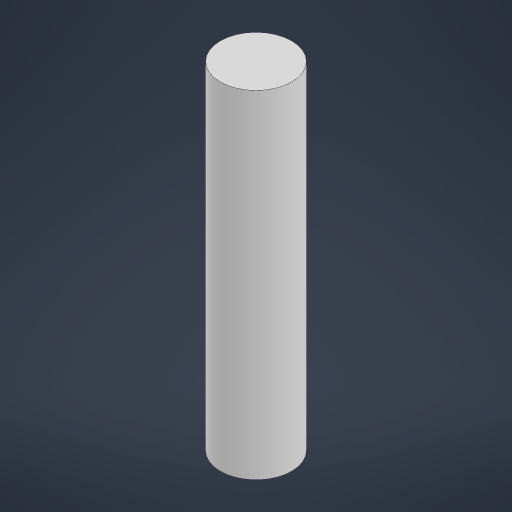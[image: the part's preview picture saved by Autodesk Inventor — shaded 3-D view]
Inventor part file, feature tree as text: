
AUTODESK INVENTOR PART (.ipt)
format: ipt  version: 2023 (Build 270158030, 158C)  size: 155,648 bytes
history: native  units: in
note: dims shown in document units (in); Inventor stores cm internally (conversion verified against a paired STEP export)
features: extrude x1, sketch x1
ambient origin geometry x8: Origin, YZ Plane, XZ Plane, XY Plane, X Axis, Y Axis, Z Axis, Center Point
bodies: Solid1 (feature_tree)
feature tree (2):
  extrude  "Extrusion1"  Depth=1.4173in TaperAngle=0.0deg
  sketch  "Sketch1"  dims[d0=0.2992in d1=1.4173in d2=0.0in]
